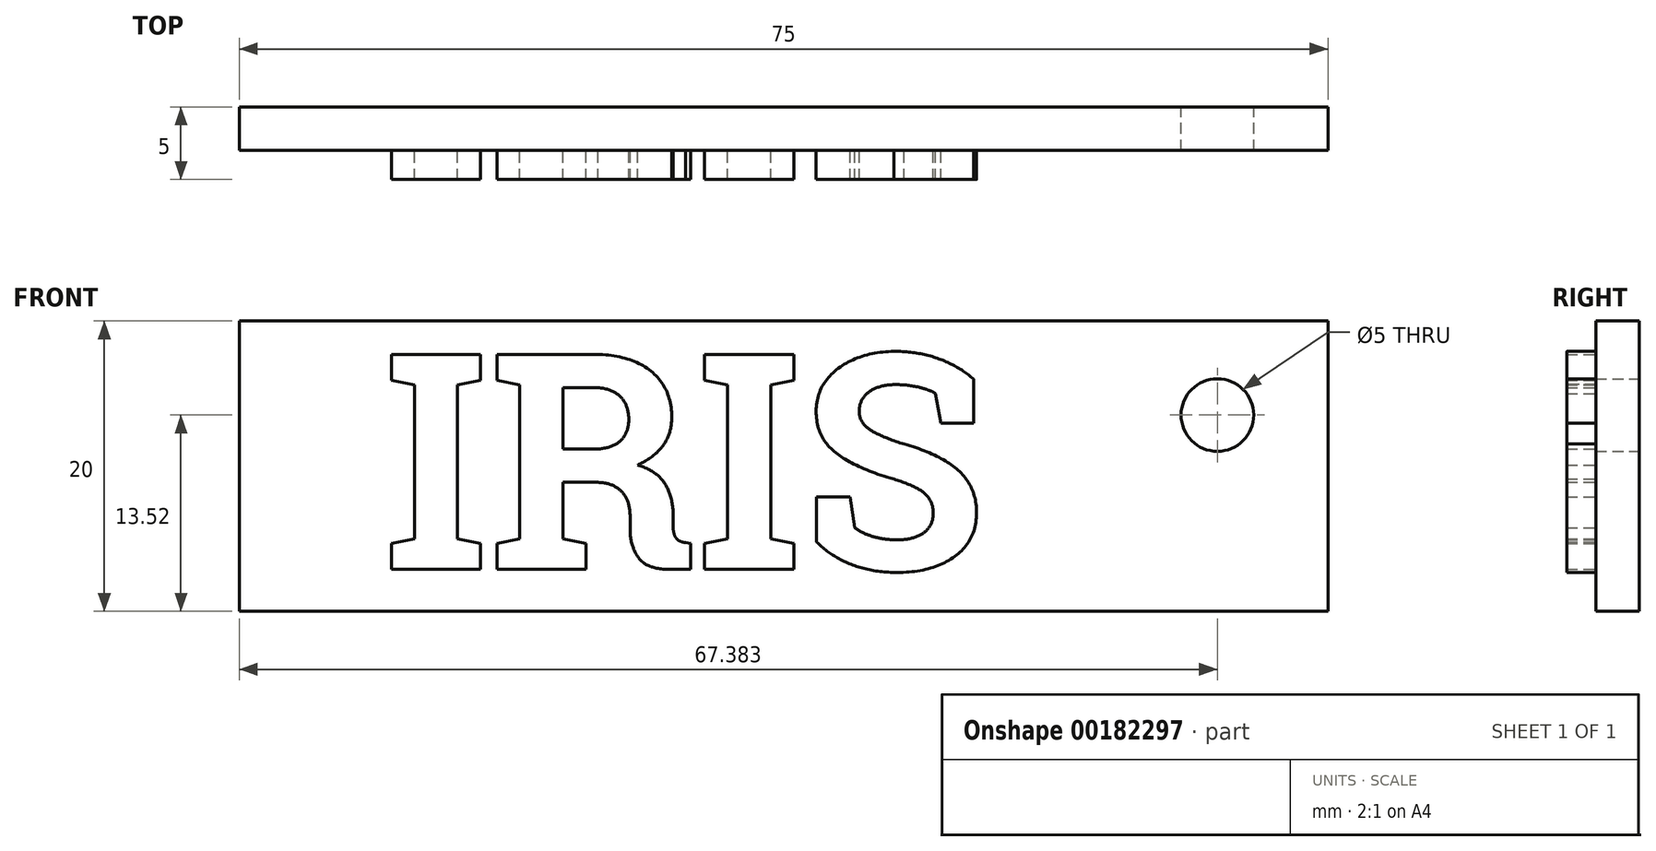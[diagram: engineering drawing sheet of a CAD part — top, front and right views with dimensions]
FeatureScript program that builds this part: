
annotation { "Feature Type Name" : "Feature", "Feature Type Description" : "" }
export const myFeature = defineFeature(function(context is Context, id is Id, definition is map)
    precondition{}
    {
        {
            var Q0;
            Q0=qCreatedBy(makeId("Front.planeOp"),FACE);
            var sketch = newSketch(context, id + "F0", { "sketchPlane" : qUnion([Q0])});
            skLineSegment(sketch, "E0.bottom", {"start": v(0, -7.31) * mm, "end": v(75, -7.31) * mm});
            skLineSegment(sketch, "E0.top", {"start": v(0, -27.31) * mm, "end": v(75, -27.31) * mm});
            skLineSegment(sketch, "E0.left", {"start": v(0, -7.31) * mm, "end": v(0, -27.31) * mm});
            skLineSegment(sketch, "E0.right", {"start": v(75, -7.31) * mm, "end": v(75, -27.31) * mm});
            skCircle(sketch, "E1", {"center": v(67.38, -13.8) * mm, "radius": 2.5 * mm});
            skSolve(sketch);
        }
        {
            var Q0;
            Q0 = qSketchRegion(id + "F0", true);
            extrude(context, id + "F1", {"entities" : qUnion([Q0]), "depth" : 3 * mm});
        }
        {
            var Q0;
            Q0=makeQuery(id+"F1.opExtrude","CAP_FACE",FACE,{"disambiguationData":[OSD([sQuery(id+"F0.wireOp",EDGE,"E0.bottom"),sQuery(id+"F0.wireOp",EDGE,"E0.top"),sQuery(id+"F0.wireOp",EDGE,"E0.left"),sQuery(id+"F0.wireOp",EDGE,"E0.right"),sQuery(id+"F0.wireOp",EDGE,"E1")])],"isStart":false});
            var sketch = newSketch(context, id + "F2", { "sketchPlane" : qUnion([Q0])});
            skText(sketch, "E2", { "text": "IRIS", "fontName": "RobotoSlab-Bold.ttf"});
            const initialGuessF2  = {"E2": [0.00993, -0.02442, 1, 0, 0.015]};
            skSetInitialGuess(sketch, initialGuessF2);
            skSolve(sketch);
        }
        {
            var Q0;
            Q0 = qSketchRegion(id + "F2", true);
            extrude(context, id + "F3", {"entities" : qUnion([Q0]), "operationType" : NewBodyOperationType.ADD, "depth" : 2 * mm});
        }
    });
